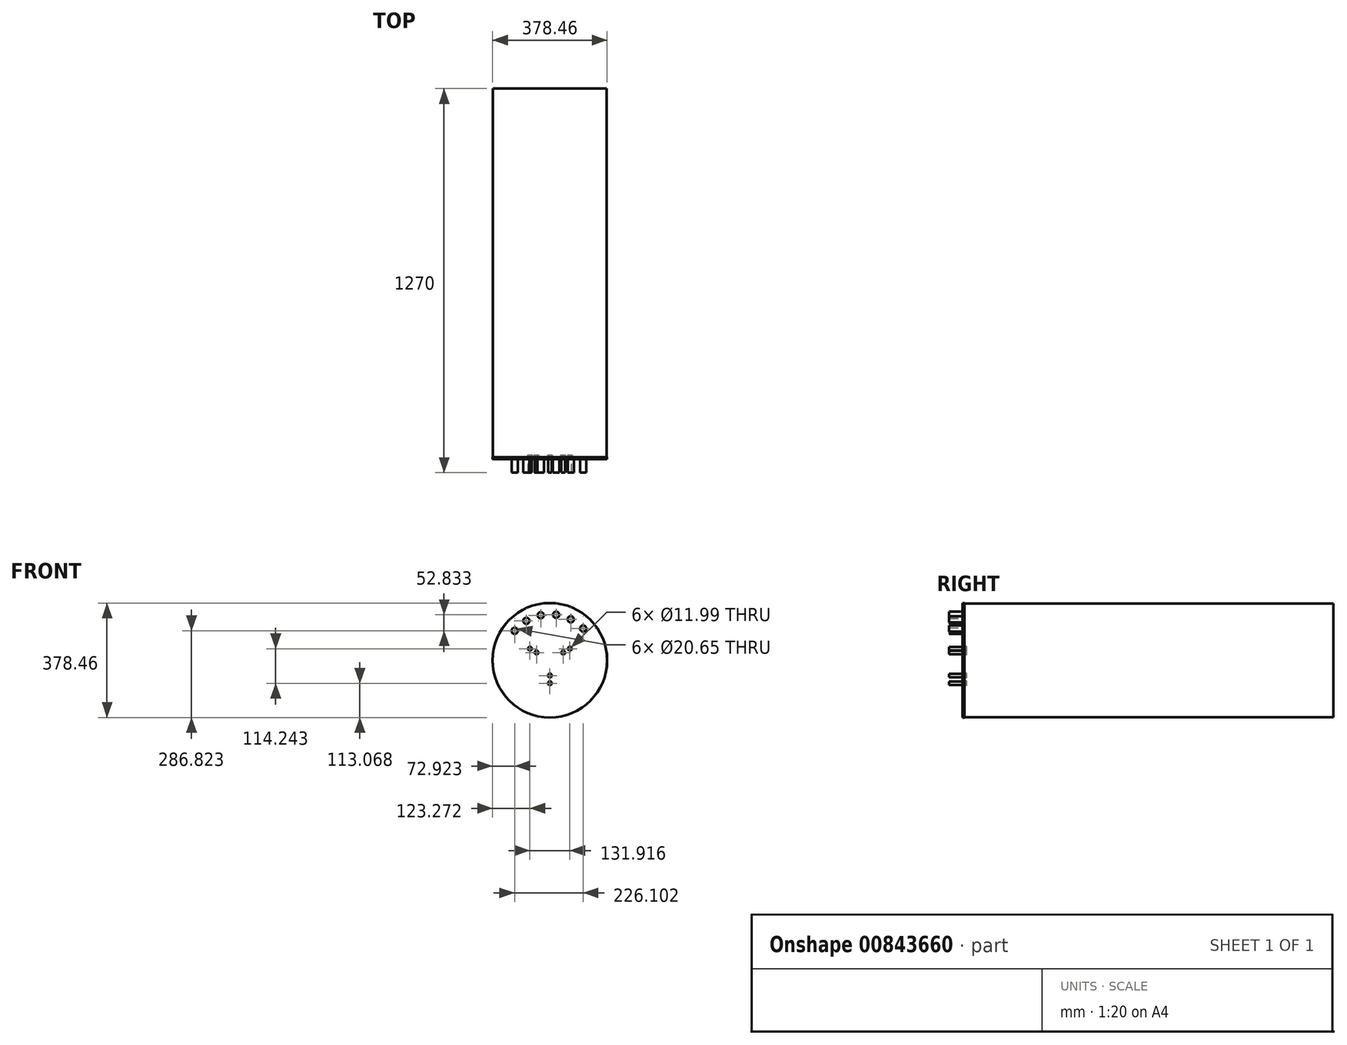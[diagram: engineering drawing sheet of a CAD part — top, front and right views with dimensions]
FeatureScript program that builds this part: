
annotation { "Feature Type Name" : "Feature", "Feature Type Description" : "" }
export const myFeature = defineFeature(function(context is Context, id is Id, definition is map)
    precondition{}
    {
        {
            var Q0;
            Q0=qCreatedBy(makeId("Front.planeOp"),FACE);
            var sketch = newSketch(context, id + "F0", { "sketchPlane" : qUnion([Q0])});
            skCircle(sketch, "E0", {"center": v(0, 0) * mm, "radius": 189.23 * mm});
            skCircle(sketch, "E1", {"center": v(0, 0) * mm, "radius": 151.83 * mm, "construction": true});
            skLineSegment(sketch, "E2", {"start": v(0, 0) * mm, "end": v(0, -325.8) * mm, "construction": true});
            skLineSegment(sketch, "E3", {"start": v(0, 0) * mm, "end": v(222.99, 128.74) * mm, "construction": true});
            skLineSegment(sketch, "E4", {"start": v(0, 0) * mm, "end": v(-282.27, 162.97) * mm, "construction": true});
            skCircle(sketch, "E5", {"center": v(43.96, 25.38) * mm, "radius": 6 * mm});
            skCircle(sketch, "E6", {"center": v(65.96, 38.08) * mm, "radius": 6 * mm});
            skCircle(sketch, "E7", {"center": v(-43.96, 25.38) * mm, "radius": 6 * mm});
            skCircle(sketch, "E8", {"center": v(-65.96, 38.08) * mm, "radius": 6 * mm});
            skCircle(sketch, "E9", {"center": v(0, -50.76) * mm, "radius": 6 * mm});
            skCircle(sketch, "E10", {"center": v(0, -76.16) * mm, "radius": 6 * mm});
            skCircle(sketch, "E11", {"center": v(-116.3, 97.6) * mm, "radius": 10.33 * mm});
            skCircle(sketch, "E12", {"center": v(-77.6, 130.5) * mm, "radius": 10.33 * mm});
            skCircle(sketch, "E13", {"center": v(-30.21, 148.8) * mm, "radius": 10.33 * mm});
            skCircle(sketch, "E14", {"center": v(20.59, 150.43) * mm, "radius": 10.33 * mm});
            skCircle(sketch, "E15", {"center": v(69.06, 135.21) * mm, "radius": 10.33 * mm});
            skCircle(sketch, "E16", {"center": v(109.8, 104.87) * mm, "radius": 10.33 * mm});
            skLineSegment(sketch, "E17", {"start": v(0, 0) * mm, "end": v(-197.05, 165.35) * mm, "construction": true});
            skSolve(sketch);
        }
        {
            var Q0;
            Q0=makeQuery(id+"F0.imprint","IMPRINT",FACE,{"disambiguationData":[TD([[makeQuery(id+"F0.imprint","IMPRINT",EDGE,{"derivedFrom":sQuery(id+"F0.wireOp",EDGE,"E0")}),1.0]])]});
            extrude(context, id + "F1", {"entities" : qUnion([Q0]), "depth" : 6.35 * mm, "offsetDistance" : 25.4 * mm});
        }
        {
            var Q0;
            Q0=makeQuery(id+"F1.opExtrude","CAP_FACE",FACE,{"disambiguationData":[OSD([sQuery(id+"F0.wireOp",EDGE,"E0"),sQuery(id+"F0.wireOp",EDGE,"E5"),sQuery(id+"F0.wireOp",EDGE,"E6"),sQuery(id+"F0.wireOp",EDGE,"E7"),sQuery(id+"F0.wireOp",EDGE,"E8"),sQuery(id+"F0.wireOp",EDGE,"E9"),sQuery(id+"F0.wireOp",EDGE,"E10"),sQuery(id+"F0.wireOp",EDGE,"E11"),sQuery(id+"F0.wireOp",EDGE,"E12"),sQuery(id+"F0.wireOp",EDGE,"E13"),sQuery(id+"F0.wireOp",EDGE,"E14"),sQuery(id+"F0.wireOp",EDGE,"E15"),sQuery(id+"F0.wireOp",EDGE,"E16")])],"isStart":true});
            var sketch = newSketch(context, id + "F2", { "sketchPlane" : qUnion([Q0])});
            skCircle(sketch, "E18", {"center": v(-65.96, 38.08) * mm, "radius": 8.26 * mm});
            skCircle(sketch, "E19", {"center": v(-43.96, 25.38) * mm, "radius": 8.26 * mm});
            skCircle(sketch, "E20", {"center": v(43.96, 25.38) * mm, "radius": 8.26 * mm});
            skCircle(sketch, "E21", {"center": v(65.96, 38.08) * mm, "radius": 8.26 * mm});
            skCircle(sketch, "E22", {"center": v(0, -50.76) * mm, "radius": 8.26 * mm});
            skCircle(sketch, "E23", {"center": v(0, -76.16) * mm, "radius": 8.26 * mm});
            skSolve(sketch);
        }
        {
            var Q0;
            Q0 = qSketchRegion(id + "F2", true);
            extrude(context, id + "F3", {"entities" : qUnion([Q0]), "depth" : 6.35 * mm, "offsetDistance" : 25.4 * mm});
        }
        {
            var Q0;
            Q0=makeQuery(id+"F3.opExtrude","CAP_FACE",FACE,{"disambiguationData":[OSD([sQuery(id+"F2.wireOp",EDGE,"E23")])],"isStart":true});
            var sketch = newSketch(context, id + "F4", { "sketchPlane" : qUnion([Q0])});
            skCircle(sketch, "E24.0", {"center": v(0, -76.16) * mm, "radius": 6 * mm});
            skCircle(sketch, "E25.0", {"center": v(0, -50.76) * mm, "radius": 6 * mm});
            skCircle(sketch, "E26.0", {"center": v(-43.96, 25.38) * mm, "radius": 6 * mm});
            skCircle(sketch, "E27.0", {"center": v(-65.96, 38.08) * mm, "radius": 6 * mm});
            skCircle(sketch, "E28.0", {"center": v(43.96, 25.38) * mm, "radius": 6 * mm});
            skCircle(sketch, "E29.0", {"center": v(65.96, 38.08) * mm, "radius": 6 * mm});
            skSolve(sketch);
        }
        {
            var Q0;
            Q0 = qSketchRegion(id + "F4", true);
            extrude(context, id + "F5", {"entities" : qUnion([Q0]), "depth" : 50.8 * mm, "offsetDistance" : 25.4 * mm});
        }
        {
            var Q0;
            Q0=makeQuery(id+"F1.opExtrude","CAP_FACE",FACE,{"disambiguationData":[OSD([sQuery(id+"F0.wireOp",EDGE,"E0"),sQuery(id+"F0.wireOp",EDGE,"E5"),sQuery(id+"F0.wireOp",EDGE,"E6"),sQuery(id+"F0.wireOp",EDGE,"E7"),sQuery(id+"F0.wireOp",EDGE,"E8"),sQuery(id+"F0.wireOp",EDGE,"E9"),sQuery(id+"F0.wireOp",EDGE,"E10"),sQuery(id+"F0.wireOp",EDGE,"E11"),sQuery(id+"F0.wireOp",EDGE,"E12"),sQuery(id+"F0.wireOp",EDGE,"E13"),sQuery(id+"F0.wireOp",EDGE,"E14"),sQuery(id+"F0.wireOp",EDGE,"E15"),sQuery(id+"F0.wireOp",EDGE,"E16")])],"isStart":true});
            var sketch = newSketch(context, id + "F6", { "sketchPlane" : qUnion([Q0])});
            skCircle(sketch, "E30.0", {"center": v(-109.8, 104.87) * mm, "radius": 10.33 * mm});
            skCircle(sketch, "E31.0", {"center": v(-69.06, 135.21) * mm, "radius": 10.33 * mm});
            skCircle(sketch, "E32.0", {"center": v(-20.59, 150.43) * mm, "radius": 10.33 * mm});
            skCircle(sketch, "E33.0", {"center": v(30.21, 148.8) * mm, "radius": 10.33 * mm});
            skCircle(sketch, "E34.0", {"center": v(77.6, 130.5) * mm, "radius": 10.33 * mm});
            skCircle(sketch, "E35.0", {"center": v(116.3, 97.6) * mm, "radius": 10.33 * mm});
            skSolve(sketch);
        }
        {
            var Q0;
            Q0 = qSketchRegion(id + "F6", true);
            extrude(context, id + "F7", {"entities" : qUnion([Q0]), "oppositeDirection" : true, "depth" : 50.8 * mm, "offsetDistance" : 25.4 * mm});
        }
        {
            var Q0;
            Q0=makeQuery(id+"F1.opExtrude","CAP_FACE",FACE,{"disambiguationData":[OSD([sQuery(id+"F0.wireOp",EDGE,"E0"),sQuery(id+"F0.wireOp",EDGE,"E5"),sQuery(id+"F0.wireOp",EDGE,"E6"),sQuery(id+"F0.wireOp",EDGE,"E7"),sQuery(id+"F0.wireOp",EDGE,"E8"),sQuery(id+"F0.wireOp",EDGE,"E9"),sQuery(id+"F0.wireOp",EDGE,"E10"),sQuery(id+"F0.wireOp",EDGE,"E11"),sQuery(id+"F0.wireOp",EDGE,"E12"),sQuery(id+"F0.wireOp",EDGE,"E13"),sQuery(id+"F0.wireOp",EDGE,"E14"),sQuery(id+"F0.wireOp",EDGE,"E15"),sQuery(id+"F0.wireOp",EDGE,"E16")])],"isStart":true});
            var sketch = newSketch(context, id + "F8", { "sketchPlane" : qUnion([Q0])});
            skCircle(sketch, "E36", {"center": v(0, 0) * mm, "radius": 187.78 * mm});
            skSolve(sketch);
        }
        {
            var Q0;
            Q0 = qSketchRegion(id + "F8", true);
            extrude(context, id + "F9", {"entities" : qUnion([Q0]), "depth" : 1219.2 * mm, "offsetDistance" : 25.4 * mm});
        }
    });
